# Revit family: Bravo
name_source: partatom
category: Mechanical Equipment
units: mm (PartAtom-declared; Revit-internal decimal feet)

## family parameters
Always vertical = Yes
Classification = None
Cut with Voids When Loaded = No
Part Type = Normal
Room Calculation Point = No
Round Connector Dimension = Use Diameter
Shared = No
Work Plane-Based = No

## types (9) — shared parameters
00_20_Manufacturer = Blauberg
00_20_Name = Extraction fan
Amperage = 0 A
Description = For round channels
Frequency = 50 Hz
Load Classification = HVAC
Maintenance zone material = <By Category>
Manufacturer = Blauberg
Number of Fase = 1
URL = https://blaubergventilatoren.de
Voltage = 230 V
zero-valued in all types: Default Elevation

## per-type parameters (varying)
| type | Apparent Load | B | Casing Material | D | Diameter | Dy | H | Height | Length | Maximum Air Flow | Power | Sound pressure level at 3 m distance | Weight | Width | c | e |
| Bravo 150 Platinum | 30 W | 205 mm  [stored 0.672572 ft] | Plastic, opaque, Platinum | 150 mm  [stored 0.492126 ft] | 150 mm  [stored 0.492126 ft] | 145 mm  [stored 0.475722 ft] | 205 mm  [stored 0.672572 ft] | 205 mm  [stored 0.672572 ft] | 143 mm  [stored 0.46916 ft] | 305.0 m³/h | 24 W | 39 dBA | 0.92 kg | 205 mm  [stored 0.672572 ft] | 124 mm  [stored 0.406824 ft] | 19 mm  [stored 0.062336 ft] |
| Bravo 100 Platinum | 21 W | 150 mm  [stored 0.492126 ft] | Plastic, opaque, Platinum | 100 mm  [stored 0.328084 ft] | 100 mm  [stored 0.328084 ft] | 95 mm  [stored 0.31168 ft] | 150 mm  [stored 0.492126 ft] | 150 mm  [stored 0.492126 ft] | 119 mm  [stored 0.39042 ft] | 101.0 m³/h | 14 W | 35 dBA | 0.58 kg | 150 mm  [stored 0.492126 ft] | 102 mm | 17 mm |
| Bravo 125 Platinum | 23 W | 176 mm  [stored 0.577428 ft] | Plastic, opaque, Platinum | 125 mm  [stored 0.410105 ft] | 125 mm  [stored 0.410105 ft] | 120 mm  [stored 0.393701 ft] | 176 mm  [stored 0.577428 ft] | 176 mm  [stored 0.577428 ft] | 121 mm  [stored 0.396982 ft] | 192.0 m³/h | 16 W | 37 dBA | 0.74 kg | 176 mm  [stored 0.577428 ft] | 104 mm | 17 mm |
| Bravo 100 Chrome | 21 W | 150 mm  [stored 0.492126 ft] | Plastic, opaque, Chrome | 100 mm  [stored 0.328084 ft] | 100 mm  [stored 0.328084 ft] | 95 mm  [stored 0.31168 ft] | 150 mm  [stored 0.492126 ft] | 150 mm  [stored 0.492126 ft] | 119 mm  [stored 0.39042 ft] | 101.0 m³/h | 14 W | 35 dBA | 0.58 kg | 150 mm  [stored 0.492126 ft] | 102 mm | 17 mm |
| Bravo 125 Chrome | 23 W | 176 mm  [stored 0.577428 ft] | Plastic, opaque, Chrome | 125 mm  [stored 0.410105 ft] | 125 mm  [stored 0.410105 ft] | 120 mm  [stored 0.393701 ft] | 176 mm  [stored 0.577428 ft] | 176 mm  [stored 0.577428 ft] | 121 mm  [stored 0.396982 ft] | 192.0 m³/h | 16 W | 37 dBA | 0.74 kg | 176 mm  [stored 0.577428 ft] | 104 mm | 17 mm |
| Bravo 150 Chrome | 30 W | 205 mm  [stored 0.672572 ft] | Plastic, opaque, Chrome | 150 mm  [stored 0.492126 ft] | 150 mm  [stored 0.492126 ft] | 145 mm  [stored 0.475722 ft] | 205 mm  [stored 0.672572 ft] | 205 mm  [stored 0.672572 ft] | 143 mm  [stored 0.46916 ft] | 305.0 m³/h | 24 W | 39 dBA | 0.92 kg | 205 mm  [stored 0.672572 ft] | 124 mm  [stored 0.406824 ft] | 19 mm  [stored 0.062336 ft] |
| Bravo 150 White | 30 W | 205 mm  [stored 0.672572 ft] | Plastic, opaque, Chrome | 150 mm  [stored 0.492126 ft] | 150 mm  [stored 0.492126 ft] | 145 mm  [stored 0.475722 ft] | 205 mm  [stored 0.672572 ft] | 205 mm  [stored 0.672572 ft] | 143 mm  [stored 0.46916 ft] | 305.0 m³/h | 24 W | 39 dBA | 0.92 kg | 205 mm  [stored 0.672572 ft] | 124 mm  [stored 0.406824 ft] | 19 mm  [stored 0.062336 ft] |
| Bravo 100 White | 21 W | 150 mm  [stored 0.492126 ft] | Plastic, opaque, white | 100 mm  [stored 0.328084 ft] | 100 mm  [stored 0.328084 ft] | 95 mm  [stored 0.31168 ft] | 150 mm  [stored 0.492126 ft] | 150 mm  [stored 0.492126 ft] | 119 mm  [stored 0.39042 ft] | 101.0 m³/h | 14 W | 35 dBA | 0.58 kg | 150 mm  [stored 0.492126 ft] | 102 mm | 17 mm |
| Bravo 125 White | 23 W | 176 mm  [stored 0.577428 ft] | Plastic, opaque, white | 125 mm  [stored 0.410105 ft] | 125 mm  [stored 0.410105 ft] | 120 mm  [stored 0.393701 ft] | 176 mm  [stored 0.577428 ft] | 176 mm  [stored 0.577428 ft] | 121 mm  [stored 0.396982 ft] | 192.0 m³/h | 16 W | 37 dBA | 0.74 kg | 176 mm  [stored 0.577428 ft] | 104 mm | 17 mm |

note: column(s) folded — value = type name in every type: 00_20_Type

note: [stored X ft] marks values corroborated as IEEE doubles in the binary element streams (Revit-internal decimal feet)
